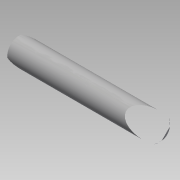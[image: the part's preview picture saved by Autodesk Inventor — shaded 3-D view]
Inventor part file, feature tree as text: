
AUTODESK INVENTOR PART (.ipt)
format: ipt  version: 2014 (Build 180170000, 170)  size: 74,752 bytes
history: native  units: mm
features: extrude x1, chamfer x1, sketch x1
ambient origin geometry x8: Origin, YZ Plane, XZ Plane, XY Plane, X Axis, Y Axis, Z Axis, Center Point
bodies: Solid1 (feature_tree)
feature tree (3):
  extrude  "Extrusion1"  Depth=15.0mm TaperAngle=0.0deg
  chamfer  "Chamfer1"  Distance=0.3mm Angle=45.0deg
  sketch  "Sketch1"  dims[d0=2.5mm d1=15.0mm d2=0.0mm d3=0.3mm d4=2.0mm d5=45.0deg]
